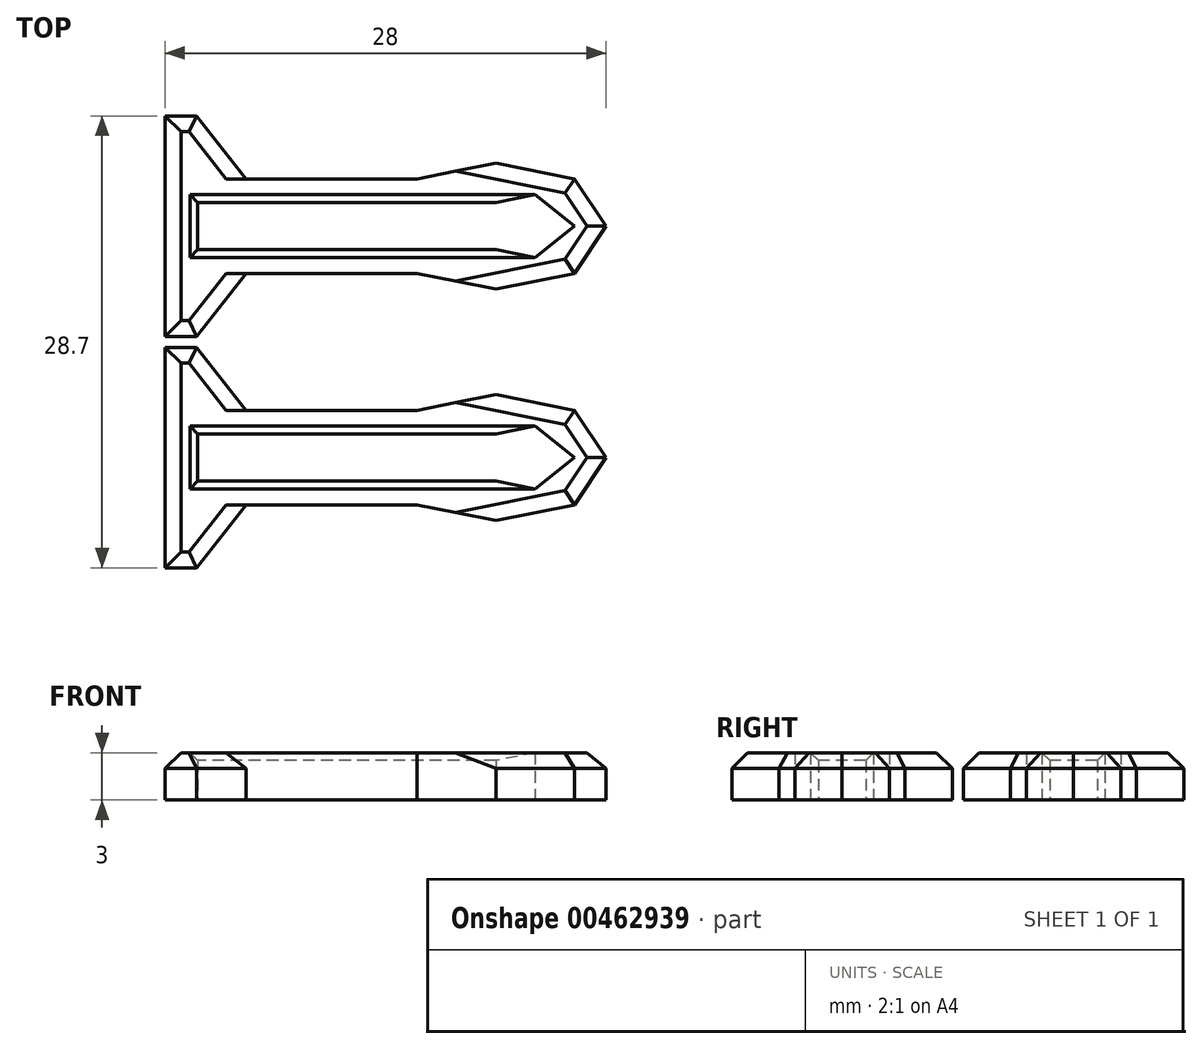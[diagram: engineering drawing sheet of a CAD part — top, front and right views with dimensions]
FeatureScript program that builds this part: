
annotation { "Feature Type Name" : "Feature", "Feature Type Description" : "" }
export const myFeature = defineFeature(function(context is Context, id is Id, definition is map)
    precondition{}
    {
        {
            var Q0;
            Q0=qCreatedBy(makeId("Top.planeOp"),FACE);
            var sketch = newSketch(context, id + "F0", { "sketchPlane" : qUnion([Q0])});
            skLineSegment(sketch, "E0.right", {"start": v(-13, -5) * mm, "end": v(-13, 9) * mm});
            skPoint(sketch, "E0.middle", {"position": v(0, 0) * mm});
            skLineSegment(sketch, "E1", {"start": v(-13, 9) * mm, "end": v(-11, 9) * mm});
            skLineSegment(sketch, "E2", {"start": v(-13, -5) * mm, "end": v(-11, -5) * mm});
            skLineSegment(sketch, "E3", {"start": v(-11, 9) * mm, "end": v(-7.86, 5) * mm});
            skLineSegment(sketch, "E4", {"start": v(-11, -5) * mm, "end": v(-7.86, -1) * mm});
            skLineSegment(sketch, "E5", {"start": v(-7.86, 5) * mm, "end": v(3, 5) * mm});
            skLineSegment(sketch, "E6", {"start": v(-7.86, -1) * mm, "end": v(3, -1) * mm});
            skLineSegment(sketch, "E7", {"start": v(13, 5) * mm, "end": v(15, 2) * mm});
            skLineSegment(sketch, "E8", {"start": v(15, 2) * mm, "end": v(13, -1) * mm});
            skLineSegment(sketch, "E9", {"start": v(-10.93, 2) * mm, "end": v(-10.93, 3.5) * mm});
            skLineSegment(sketch, "E10", {"start": v(-10.93, 2) * mm, "end": v(-10.93, 0.5) * mm});
            skLineSegment(sketch, "E11", {"start": v(-10.93, 3.5) * mm, "end": v(3, 3.5) * mm});
            skLineSegment(sketch, "E12", {"start": v(-10.93, 0.5) * mm, "end": v(3, 0.5) * mm});
            skLineSegment(sketch, "E13", {"start": v(10.5, 4) * mm, "end": v(13, 2) * mm});
            skLineSegment(sketch, "E14", {"start": v(13, 2) * mm, "end": v(10.5, 0) * mm});
            skPoint(sketch, "E15", {"position": v(8, 3.5) * mm});
            skPoint(sketch, "E16", {"position": v(8, 0.5) * mm});
            skLineSegment(sketch, "E17", {"start": v(10.5, 4) * mm, "end": v(8, 3.5) * mm});
            skLineSegment(sketch, "E18", {"start": v(3, 3.5) * mm, "end": v(8, 3.5) * mm});
            skLineSegment(sketch, "E19", {"start": v(3, 0.5) * mm, "end": v(8, 0.5) * mm});
            skLineSegment(sketch, "E20", {"start": v(10.5, 0) * mm, "end": v(8, 0.5) * mm});
            skLineSegment(sketch, "E21", {"start": v(3, -1) * mm, "end": v(8, -2) * mm});
            skLineSegment(sketch, "E22", {"start": v(8, -2) * mm, "end": v(13, -1) * mm});
            skLineSegment(sketch, "E23", {"start": v(3, 5) * mm, "end": v(8, 6) * mm});
            skLineSegment(sketch, "E24", {"start": v(13, 5) * mm, "end": v(8, 6) * mm});
            skSolve(sketch);
        }
        {
            var Q0;
            Q0=makeQuery(id+"F0.imprint","IMPRINT",FACE,{"disambiguationData":[TD([[makeQuery(id+"F0.imprint","IMPRINT",EDGE,{"derivedFrom":sQuery(id+"F0.wireOp",EDGE,"E0.right")}),-1.0]])]});
            extrude(context, id + "F1", {"entities" : qUnion([Q0]), "depth" : 3 * mm});
        }
        {
            var Q0;
            Q0=makeQuery(id+"F1.opExtrude","CAP_EDGE",EDGE,{"disambiguationData":[OSD([sQuery(id+"F0.wireOp",EDGE,"E2")])],"isStart":false});
            var Q1;
            Q1=makeQuery(id+"F1.opExtrude","CAP_EDGE",EDGE,{"disambiguationData":[OSD([sQuery(id+"F0.wireOp",EDGE,"E0.right")])],"isStart":false});
            var Q2;
            Q2=makeQuery(id+"F1.opExtrude","CAP_EDGE",EDGE,{"disambiguationData":[OSD([sQuery(id+"F0.wireOp",EDGE,"E1")])],"isStart":false});
            var Q3;
            Q3=makeQuery(id+"F1.opExtrude","CAP_EDGE",EDGE,{"disambiguationData":[OSD([sQuery(id+"F0.wireOp",EDGE,"E3")])],"isStart":false});
            var Q4;
            Q4=makeQuery(id+"F1.opExtrude","CAP_EDGE",EDGE,{"disambiguationData":[OSD([sQuery(id+"F0.wireOp",EDGE,"RiCfIarJ-YTI8-ext0-GKhL-THrZ4bTmaygU")])],"isStart":false});
            var Q5;
            Q5=makeQuery(id+"F1.opExtrude","CAP_EDGE",EDGE,{"disambiguationData":[OSD([sQuery(id+"F0.wireOp",EDGE,"pVfzpj9u-kBFY-9iYZ-UWUw-bZWDQn1kEbCG")])],"isStart":false});
            var Q6;
            Q6=makeQuery(id+"F1.opExtrude","CAP_EDGE",EDGE,{"disambiguationData":[OSD([sQuery(id+"F0.wireOp",EDGE,"E7")])],"isStart":false});
            var Q7;
            Q7=makeQuery(id+"F1.opExtrude","CAP_EDGE",EDGE,{"disambiguationData":[OSD([sQuery(id+"F0.wireOp",EDGE,"E8")])],"isStart":false});
            var Q8;
            Q8=makeQuery(id+"F1.opExtrude","CAP_EDGE",EDGE,{"disambiguationData":[OSD([sQuery(id+"F0.wireOp",EDGE,"uUdRNzHu-j5Ha-TmUZ-sETp-g5ialT0z3Oa5")])],"isStart":false});
            var Q9;
            Q9=makeQuery(id+"F1.opExtrude","CAP_EDGE",EDGE,{"disambiguationData":[OSD([sQuery(id+"F0.wireOp",EDGE,"toTlb6GJ-4URF-8bO6-I1nD-Q2SlnhyXj9vE")])],"isStart":false});
            var Q10;
            Q10=makeQuery(id+"F1.opExtrude","CAP_EDGE",EDGE,{"disambiguationData":[OSD([sQuery(id+"F0.wireOp",EDGE,"E4")])],"isStart":false});
            var Q11;
            Q11=makeQuery(id+"F1.opExtrude","CAP_EDGE",EDGE,{"disambiguationData":[OSD([sQuery(id+"F0.wireOp",EDGE,"pe4MHGRj-pC2t-OOTb-gnea-0pZkdEg2MQeR")])],"isStart":false});
            var Q12;
            Q12=makeQuery(id+"F1.opExtrude","CAP_EDGE",EDGE,{"disambiguationData":[OSD([sQuery(id+"F0.wireOp",EDGE,"D9QuzVbn-0BOK-cFoe-iw7o-LN2DakbSObOS")])],"isStart":false});
            var Q13;
            Q13=makeQuery(id+"F1.opExtrude","CAP_EDGE",EDGE,{"disambiguationData":[OSD([sQuery(id+"F0.wireOp",EDGE,"mzJ8t0nO-NYMU-p95C-X1FF-HxI7hO6F6wAo")])],"isStart":false});
            var Q14;
            Q14=makeQuery(id+"F1.opExtrude","CAP_EDGE",EDGE,{"disambiguationData":[OSD([sQuery(id+"F0.wireOp",EDGE,"AegdE7PK-5HoD-yF8r-xzF3-XIRHWE2Vfr4x")])],"isStart":false});
            var Q15;
            Q15=makeQuery(id+"F1.opExtrude","CAP_EDGE",EDGE,{"disambiguationData":[OSD([sQuery(id+"F0.wireOp",EDGE,"E24")])],"isStart":false});
            var Q16;
            Q16=makeQuery(id+"F1.opExtrude","CAP_EDGE",EDGE,{"disambiguationData":[OSD([sQuery(id+"F0.wireOp",EDGE,"E22")])],"isStart":false});
            chamfer(context, id + "F2", {"entities" : qUnion([Q0, Q1, Q2, Q3, Q4, Q5, Q6, Q7, Q8, Q9, Q10, Q11, Q12, Q13, Q14, Q15, Q16]), "width" : 1 * mm, "tangentPropagation" : true});
        }
        {
            var Q0;
            Q0=makeQuery(id+"F1.opExtrude","CAP_EDGE",EDGE,{"disambiguationData":[OSD([sQuery(id+"F0.wireOp",EDGE,"E11")])],"isStart":false});
            var Q1;
            Q1=makeQuery(id+"F1.opExtrude","CAP_EDGE",EDGE,{"disambiguationData":[OSD([sQuery(id+"F0.wireOp",EDGE,"E12")])],"isStart":false});
            var Q2;
            Q2=makeQuery(id+"F1.opExtrude","CAP_EDGE",EDGE,{"disambiguationData":[OSD([sQuery(id+"F0.wireOp",EDGE,"E9"),sQuery(id+"F0.wireOp",EDGE,"E10")])],"isStart":false});
            chamfer(context, id + "F3", {"entities" : qUnion([Q0, Q1, Q2]), "width" : .5 * mm, "tangentPropagation" : true});
        }
        {
            var Q0;
            Q0=makeQuery(id+"F1.opExtrude","SWEPT_BODY",BODY,{"disambiguationData":[OSD([sQuery(id+"F0.wireOp",EDGE,"E0.right"),sQuery(id+"F0.wireOp",EDGE,"E1"),sQuery(id+"F0.wireOp",EDGE,"E2"),sQuery(id+"F0.wireOp",EDGE,"E3"),sQuery(id+"F0.wireOp",EDGE,"E4"),sQuery(id+"F0.wireOp",EDGE,"E5"),sQuery(id+"F0.wireOp",EDGE,"E6"),sQuery(id+"F0.wireOp",EDGE,"RiCfIarJ-YTI8-ext0-GKhL-THrZ4bTmaygU"),sQuery(id+"F0.wireOp",EDGE,"pVfzpj9u-kBFY-9iYZ-UWUw-bZWDQn1kEbCG"),sQuery(id+"F0.wireOp",EDGE,"toTlb6GJ-4URF-8bO6-I1nD-Q2SlnhyXj9vE"),sQuery(id+"F0.wireOp",EDGE,"uUdRNzHu-j5Ha-TmUZ-sETp-g5ialT0z3Oa5"),sQuery(id+"F0.wireOp",EDGE,"E7"),sQuery(id+"F0.wireOp",EDGE,"E8"),sQuery(id+"F0.wireOp",EDGE,"E9"),sQuery(id+"F0.wireOp",EDGE,"E10"),sQuery(id+"F0.wireOp",EDGE,"E11"),sQuery(id+"F0.wireOp",EDGE,"E12"),sQuery(id+"F0.wireOp",EDGE,"sPvlMwZL-jHLV-RGcl-EZEG-XYItofmvpDPV"),sQuery(id+"F0.wireOp",EDGE,"cug3Qfaj-IO6r-07Ia-n4Uv-iqhHHkDEEDpZ"),sQuery(id+"F0.wireOp",EDGE,"KtJLeM3E-bWsT-YREb-ERAc-HM8mOg3JTNo2"),sQuery(id+"F0.wireOp",EDGE,"E13"),sQuery(id+"F0.wireOp",EDGE,"E14"),sQuery(id+"F0.wireOp",EDGE,"Ts7GWlPn-JgMu-sYLu-GEfH-XaRjhSBGqaNS")])]});
            transform(context, id + "F4", {"entities" : qUnion([Q0]), "transformType" : TransformType.TRANSLATION_3D, "dx" : 0 * mm, "dy" : -14.7 * mm, "dz" : 0 * mm, "makeCopy" : true});
        }
    });
